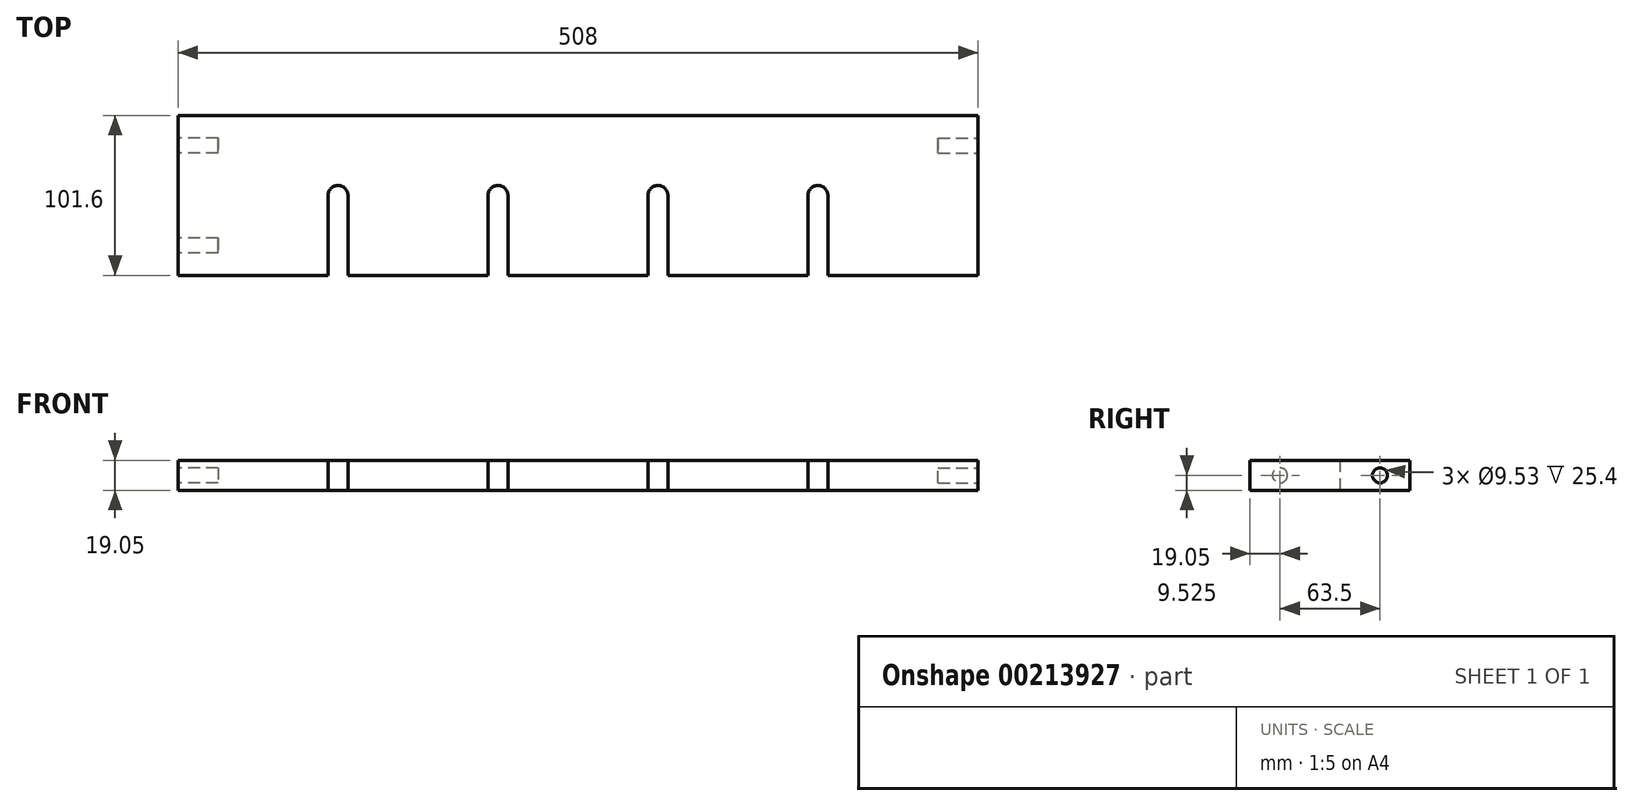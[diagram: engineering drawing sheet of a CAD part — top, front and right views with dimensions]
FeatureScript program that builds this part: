
annotation { "Feature Type Name" : "Feature", "Feature Type Description" : "" }
export const myFeature = defineFeature(function(context is Context, id is Id, definition is map)
    precondition{}
    {
        {
            var Q0;
            Q0=qCreatedBy(makeId("Top.planeOp"),FACE);
            var sketch = newSketch(context, id + "F0", { "sketchPlane" : qUnion([Q0])});
            skLineSegment(sketch, "E0.bottom", {"start": v(254, 50.8) * mm, "end": v(-254, 50.8) * mm});
            skLineSegment(sketch, "E0.left", {"start": v(254, 50.8) * mm, "end": v(254, -50.8) * mm});
            skLineSegment(sketch, "E0.right", {"start": v(-254, 50.8) * mm, "end": v(-254, -50.8) * mm});
            skLineSegment(sketch, "E1", {"start": v(-254, -50.8) * mm, "end": v(-158.75, -50.8) * mm});
            skLineSegment(sketch, "E2.left", {"start": v(-158.75, -50.8) * mm, "end": v(-158.75, 0) * mm});
            skLineSegment(sketch, "E2.right", {"start": v(-146.05, -50.8) * mm, "end": v(-146.05, 0) * mm});
            skArc(sketch, "E3", {"start": v(-146.05, 0) * mm, "mid": v(-152.4, 6.35) * mm, "end": v(-158.75, 0) * mm});
            skLineSegment(sketch, "E4.1.0.0", {"start": v(-57.15, -50.8) * mm, "end": v(-57.15, 0) * mm});
            skLineSegment(sketch, "E4.1.0.1", {"start": v(-44.45, -50.8) * mm, "end": v(-44.45, 0) * mm});
            skArc(sketch, "E4.1.0.2", {"start": v(-44.45, 0) * mm, "mid": v(-50.8, 6.35) * mm, "end": v(-57.15, 0) * mm});
            skLineSegment(sketch, "E4.2.0.0", {"start": v(44.45, -50.8) * mm, "end": v(44.45, 0) * mm});
            skLineSegment(sketch, "E4.2.0.1", {"start": v(57.15, -50.8) * mm, "end": v(57.15, 0) * mm});
            skArc(sketch, "E4.2.0.2", {"start": v(57.15, 0) * mm, "mid": v(50.8, 6.35) * mm, "end": v(44.45, 0) * mm});
            skLineSegment(sketch, "E4.3.0.0", {"start": v(146.05, -50.8) * mm, "end": v(146.05, 0) * mm});
            skLineSegment(sketch, "E4.3.0.1", {"start": v(158.75, -50.8) * mm, "end": v(158.75, 0) * mm});
            skArc(sketch, "E4.3.0.2", {"start": v(158.75, 0) * mm, "mid": v(152.4, 6.35) * mm, "end": v(146.05, 0) * mm});
            skLineSegment(sketch, "E4.direction1", {"start": v(-146.05, -50.8) * mm, "end": v(-57.15, -50.8) * mm, "construction": true});
            skLineSegment(sketch, "E5.trimOffspring", {"start": v(-44.45, -50.8) * mm, "end": v(44.45, -50.8) * mm});
            skLineSegment(sketch, "E6.trimOffspring", {"start": v(57.15, -50.8) * mm, "end": v(146.05, -50.8) * mm});
            skLineSegment(sketch, "E7.trimOffspring", {"start": v(158.75, -50.8) * mm, "end": v(254, -50.8) * mm});
            skLineSegment(sketch, "E8.trimOffspring", {"start": v(-146.05, -50.8) * mm, "end": v(-57.15, -50.8) * mm});
            skSolve(sketch);
        }
        {
            var Q0;
            Q0=makeQuery(id+"F0.imprint","IMPRINT",FACE,{"disambiguationData":[TD([[makeQuery(id+"F0.imprint","IMPRINT",EDGE,{"derivedFrom":sQuery(id+"F0.wireOp",EDGE,"E0.bottom")}),1.0]])]});
            extrude(context, id + "F1", {"entities" : qUnion([Q0]), "depth" : 19.05 * mm});
        }
        {
            var Q0;
            Q0=makeQuery(id+"F1.opExtrude","SWEPT_FACE",FACE,{"disambiguationData":[OSD([sQuery(id+"F0.wireOp",EDGE,"E0.left")])]});
            var sketch = newSketch(context, id + "F2", { "sketchPlane" : qUnion([Q0])});
            skCircle(sketch, "E9", {"center": v(31.75, 9.53) * mm, "radius": 4.76 * mm});
            skSolve(sketch);
        }
        {
            var Q0;
            Q0 = qSketchRegion(id + "F2", true);
            extrude(context, id + "F3", {"entities" : qUnion([Q0]), "operationType" : NewBodyOperationType.REMOVE, "oppositeDirection" : true, "depth" : 25.4 * mm});
        }
        {
            var Q0;
            Q0=makeQuery(id+"F1.opExtrude","SWEPT_FACE",FACE,{"disambiguationData":[OSD([sQuery(id+"F0.wireOp",EDGE,"E0.right")])]});
            var sketch = newSketch(context, id + "F4", { "sketchPlane" : qUnion([Q0])});
            skCircle(sketch, "E10", {"center": v(-31.75, 9.52) * mm, "radius": 4.76 * mm});
            skCircle(sketch, "E11.1.0.0", {"center": v(31.75, 9.53) * mm, "radius": 4.76 * mm});
            skLineSegment(sketch, "E11.direction1", {"start": v(-31.75, 9.52) * mm, "end": v(31.75, 9.53) * mm, "construction": true});
            skSolve(sketch);
        }
        {
            var Q0;
            Q0 = qSketchRegion(id + "F4", true);
            extrude(context, id + "F5", {"entities" : qUnion([Q0]), "operationType" : NewBodyOperationType.REMOVE, "oppositeDirection" : true, "depth" : 25.4 * mm});
        }
    });
